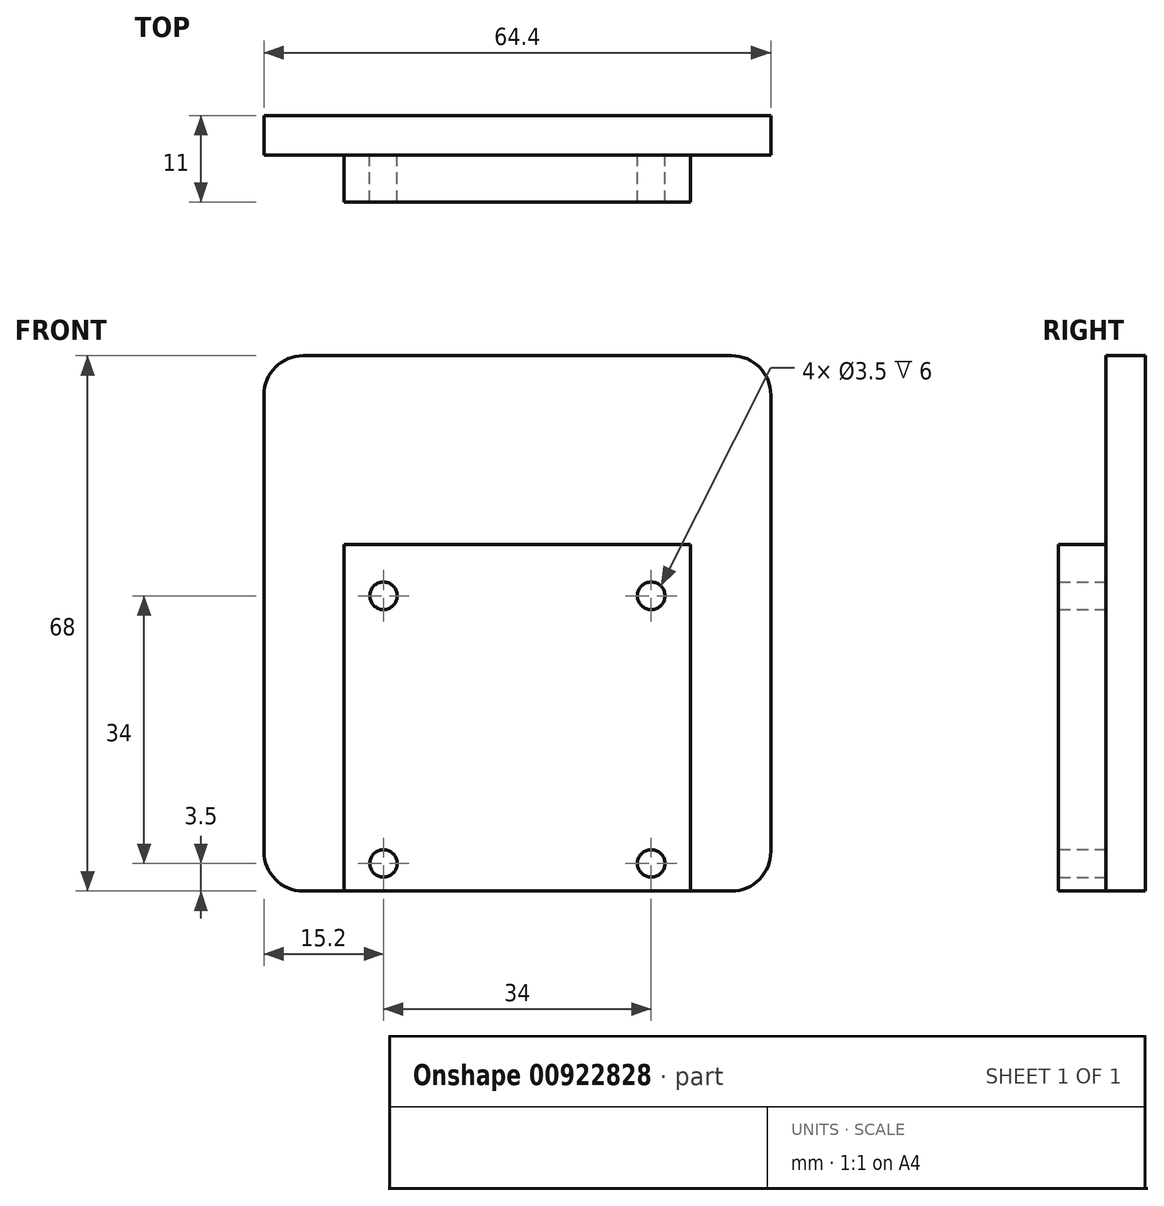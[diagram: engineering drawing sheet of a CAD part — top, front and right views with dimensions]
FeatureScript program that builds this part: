
annotation { "Feature Type Name" : "Feature", "Feature Type Description" : "" }
export const myFeature = defineFeature(function(context is Context, id is Id, definition is map)
    precondition{}
    {
        {
            var Q0;
            Q0=qCreatedBy(makeId("Front.planeOp"),FACE);
            var sketch = newSketch(context, id + "F0", { "sketchPlane" : qUnion([Q0])});
            skLineSegment(sketch, "E0.bottom", {"start": v(-27.2, 34) * mm, "end": v(27.2, 34) * mm});
            skLineSegment(sketch, "E0.top", {"start": v(-27.2, -34) * mm, "end": v(27.2, -34) * mm});
            skLineSegment(sketch, "E0.left", {"start": v(-32.2, 29) * mm, "end": v(-32.2, -29) * mm});
            skLineSegment(sketch, "E0.right", {"start": v(32.2, 29) * mm, "end": v(32.2, -29) * mm});
            skPoint(sketch, "E0.middle", {"position": v(0, 0) * mm});
            skPoint(sketch, "E1.visualSharp", {"position": v(-32.2, 34) * mm});
            skArc(sketch, "E1.filletArc", {"start": v(-27.2, 34) * mm, "mid": v(-30.74, 32.54) * mm, "end": v(-32.2, 29) * mm});
            skPoint(sketch, "E2.visualSharp", {"position": v(-32.2, -34) * mm});
            skArc(sketch, "E2.filletArc", {"start": v(-32.2, -29) * mm, "mid": v(-30.74, -32.54) * mm, "end": v(-27.2, -34) * mm});
            skPoint(sketch, "E3.visualSharp", {"position": v(32.2, -34) * mm});
            skArc(sketch, "E3.filletArc", {"start": v(27.2, -34) * mm, "mid": v(30.74, -32.54) * mm, "end": v(32.2, -29) * mm});
            skPoint(sketch, "E4.visualSharp", {"position": v(32.2, 34) * mm});
            skArc(sketch, "E4.filletArc", {"start": v(32.2, 29) * mm, "mid": v(30.74, 32.54) * mm, "end": v(27.2, 34) * mm});
            skSolve(sketch);
        }
        {
            var Q0;
            Q0 = qSketchRegion(id + "F0", true);
            extrude(context, id + "F1", {"entities" : qUnion([Q0]), "oppositeDirection" : true, "depth" : 5 * mm, "offsetDistance" : 25 * mm});
        }
        {
            var Q0;
            Q0=makeQuery(id+"F1.opExtrude","CAP_FACE",FACE,{"disambiguationData":[OSD([sQuery(id+"F0.wireOp",EDGE,"E0.bottom"),sQuery(id+"F0.wireOp",EDGE,"E0.top"),sQuery(id+"F0.wireOp",EDGE,"E0.left"),sQuery(id+"F0.wireOp",EDGE,"E0.right"),sQuery(id+"F0.wireOp",EDGE,"E1.filletArc"),sQuery(id+"F0.wireOp",EDGE,"E2.filletArc"),sQuery(id+"F0.wireOp",EDGE,"E3.filletArc"),sQuery(id+"F0.wireOp",EDGE,"E4.filletArc")])],"isStart":true});
            var sketch = newSketch(context, id + "F2", { "sketchPlane" : qUnion([Q0])});
            skLineSegment(sketch, "E5", {"start": v(0, 18.76) * mm, "end": v(0, -34) * mm, "construction": true});
            skLineSegment(sketch, "E6.bottom", {"start": v(0, -34) * mm, "end": v(-22, -34) * mm});
            skLineSegment(sketch, "E6.top", {"start": v(0, 10) * mm, "end": v(-22, 10) * mm});
            skLineSegment(sketch, "E6.left", {"start": v(0, -34) * mm, "end": v(0, 10) * mm});
            skLineSegment(sketch, "E6.right", {"start": v(-22, -34) * mm, "end": v(-22, 10) * mm});
            skCircle(sketch, "E7", {"center": v(-17, -30.5) * mm, "radius": 1.75 * mm});
            skLineSegment(sketch, "E8", {"start": v(0, -13.5) * mm, "end": v(-22, -13.5) * mm, "construction": true});
            skCircle(sketch, "E9.MirrorC", {"center": v(-17, 3.5) * mm, "radius": 1.75 * mm});
            skCircle(sketch, "E10.MirrorC", {"center": v(17, 3.5) * mm, "radius": 1.75 * mm});
            skLineSegment(sketch, "E11.MirrorCS", {"start": v(0, 10) * mm, "end": v(22, 10) * mm});
            skLineSegment(sketch, "E12.MirrorCS", {"start": v(22, -34) * mm, "end": v(22, 10) * mm});
            skLineSegment(sketch, "E13.MirrorCS", {"start": v(0, -34) * mm, "end": v(22, -34) * mm});
            skCircle(sketch, "E14.MirrorC", {"center": v(17, -30.5) * mm, "radius": 1.75 * mm});
            skSolve(sketch);
        }
        {
            var Q0;
            Q0 = qSketchRegion(id + "F2", true);
            extrude(context, id + "F3", {"entities" : qUnion([Q0]), "operationType" : NewBodyOperationType.ADD, "depth" : 6 * mm, "offsetDistance" : 25 * mm});
        }
    });
